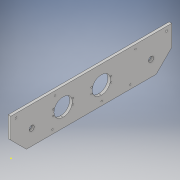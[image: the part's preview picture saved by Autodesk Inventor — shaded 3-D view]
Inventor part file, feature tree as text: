
AUTODESK INVENTOR PART (.ipt)
format: ipt  version: 2017 (Build 210142000, 142)  size: 219,136 bytes
history: native  units: in
note: dims shown in document units (in); Inventor stores cm internally (conversion verified against a paired STEP export)
features: sketch x12, hole x8, extrude x2, chamfer x2, thicken_offset x1, projected_geometry x1
ambient origin geometry x8: Origin, YZ Plane, XZ Plane, XY Plane, X Axis, Y Axis, Z Axis, Center Point
bodies: Solid1 (feature_tree)
feature tree (26):
  extrude  "Extrusion1"  Depth=15.5in
  sketch  "Sketch3"  dims[d4=2.0in]
  sketch  "Sketch4"  dims[d5=1.0in]
  chamfer  "Chamfer1"  Distance=0.25in
  chamfer  "Chamfer2"  Distance=1.5in Angle=45.0deg
  hole  "Hole1"  [1 undecoded]
  hole  "Hole3"  [1 undecoded]
  sketch  "Sketch8"  dims[d13=1.5in d14=0.125in d15=45.0deg d16=2.0in]
  hole  "Hole4"  [1 undecoded]
  hole  "Hole6"  [1 undecoded]
  extrude  "Extrusion2"  Depth=0.5in
  thicken_offset  "Thicken1"
  sketch  "Sketch16"  dims[d20=0.501in d21=0.75in d22=0.375in d23=0.25in d24=0.5635in d25=1.0in d26=0.8108in d42=0.394in]
  sketch  "Sketch17"  dims[d43=3.75in d44=3.75in]
  sketch  "Sketch18"  dims[d45=0.144in d46=0.5in]
  hole  "Hole10"  [1 undecoded]
  hole  "Hole11"  [1 undecoded]
  hole  "Hole12"  [1 undecoded]
  hole  "Hole13"  [1 undecoded]
  sketch  "Sketch19"  dims[d47=0.5in d48=0.188in d49=0.75in d50=0.375in d51=0.25in d52=0.5635in d53=1.0in d54=0.8108in d57=0.394in d61=0.14in d62=0.75in d63=0.375in d64=0.25in d65=0.5635in d66=1.0in d67=0.8108in d75=1.7in d76=0.75in d77=0.375in d78=0.25in d79=0.5635in d80=1.0in d81=0.8108in d82=0.144in d108=1.5in d109=1.5in d113=0.945in d114=0.276in d115=0.276in d116=0.945in d117=0.945in d118=0.945in d119=0.138in d120=0.138in d121=0.138in d122=0.138in d123=0.138in d124=1.0in d125=0.0in d128=8.75in d129=0.25in d130=0.25in d131=0.4in d132=0.4in d133=3.0in d135=0.14in d136=3.5in d138=0.14in d139=0.394in d141=4.0in d143=4.0in d145=0.188in d146=0.188in d147=0.14in d148=0.75in d149=0.375in d150=0.25in d151=0.5635in d152=1.0in d153=0.8108in d154=0.14in d155=0.75in d156=0.375in d157=0.25in d158=0.5635in d159=1.0in d160=0.8108in d161=0.14in d162=0.75in d163=0.375in d164=0.25in d165=0.5635in d166=1.0in d167=0.8108in d168=0.14in d169=0.75in d170=0.375in d171=0.25in d172=0.5635in d173=1.0in d174=0.8108in d177=1.0in d178=1.0in]
  sketch  "Sketch1"  dims[d2=3.25in d3=15.5in]
  sketch  "Sketch5"  dims[d6=2.0in]
  projected_geometry  "Projected Loop1"
  sketch  "Sketch7"  dims[d7=1.0in d8=0.25in d9=0.0in d10=1.5in d11=0.125in d12=45.0deg]
  sketch  "Sketch10"  dims[d17=1.5in d18=1.5in]
  sketch  "Sketch14"  dims[d19=2.0in]
note: 8 required parameter values undecoded (feature->parameter linkage not recoverable at this tier; creation-order binding heuristic only, values carry confidence <= 0.55)
